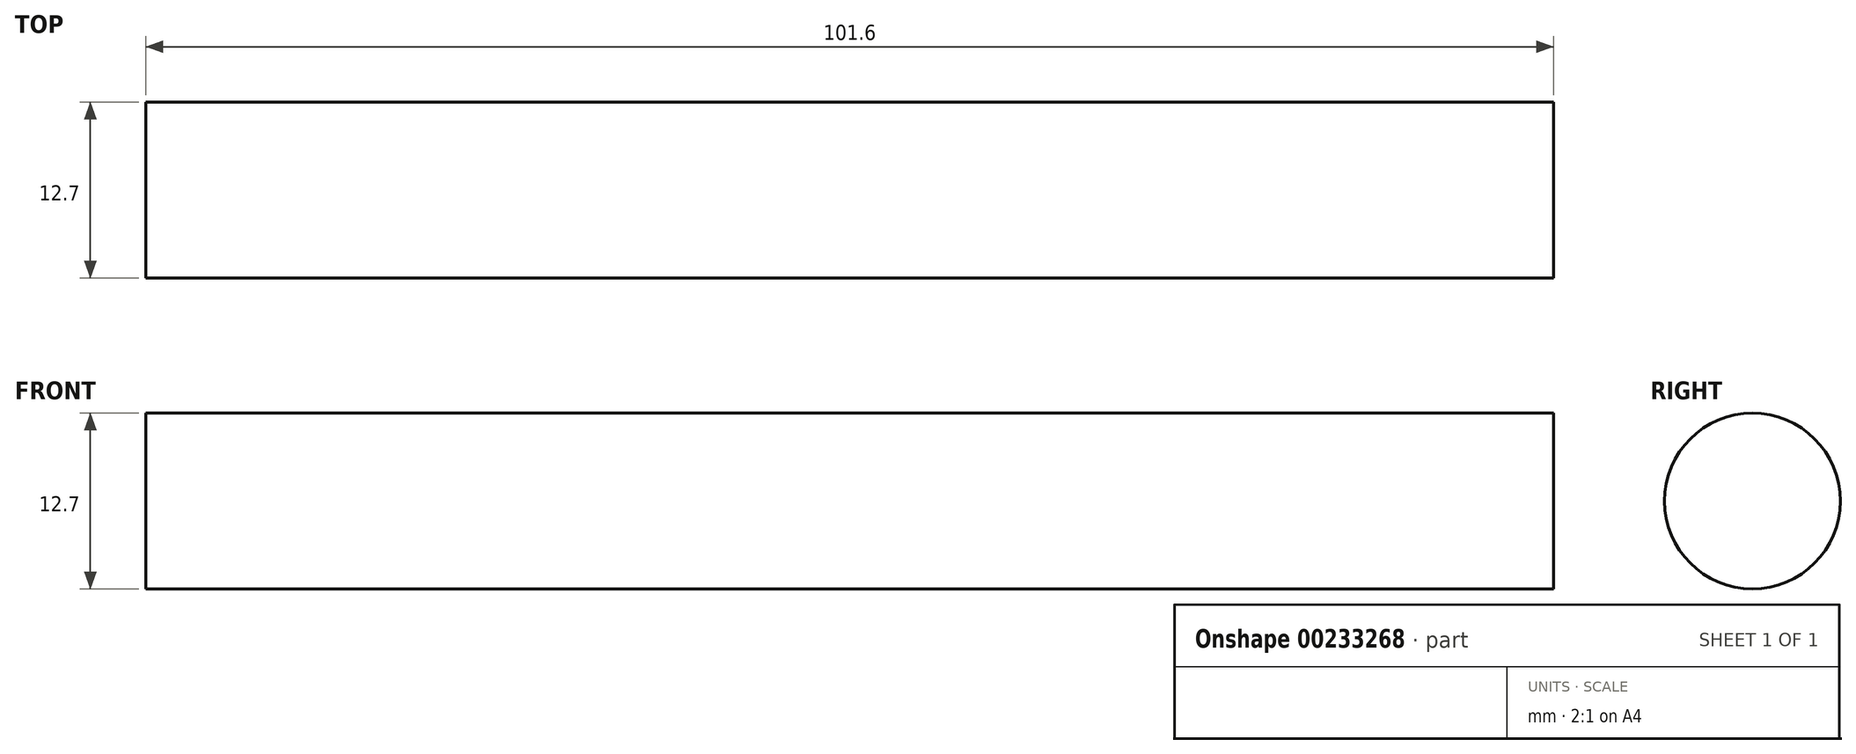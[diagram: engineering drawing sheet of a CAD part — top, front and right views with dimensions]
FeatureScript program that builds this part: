
annotation { "Feature Type Name" : "Feature", "Feature Type Description" : "" }
export const myFeature = defineFeature(function(context is Context, id is Id, definition is map)
    precondition{}
    {
        {
            var Q0;
            Q0=qCreatedBy(makeId("Right.planeOp"),FACE);
            var sketch = newSketch(context, id + "F0", { "sketchPlane" : qUnion([Q0])});
            skCircle(sketch, "E0", {"center": v(-16.26, 22.97) * mm, "radius": 6.35 * mm});
            skSolve(sketch);
        }
        {
            var Q0;
            Q0 = qSketchRegion(id + "F0", true);
            extrude(context, id + "F1", {"entities" : qUnion([Q0]), "depth" : 101.6 * mm});
        }
    });
